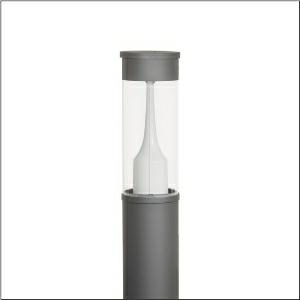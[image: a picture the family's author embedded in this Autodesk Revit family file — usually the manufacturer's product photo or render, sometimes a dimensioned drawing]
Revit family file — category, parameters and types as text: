
# Revit family: city-light_260_iq___st1_2a_5xa5295af14h_a960
name_source: partatom
category: Lighting Fixtures
units: mm (PartAtom-declared; Revit-internal decimal feet)

## family parameters
Cut with Voids When Loaded = No
Host = Face
Light Source = No
Part Type = Normal
Room Calculation Point = No
Round Connector Dimension = Use Diameter
Shared = No

## types (1)
- --- (1 x LED, 1540 lm, 12.9 W, 2200K)
    Apparent Load = 13 VA
    CIE Flux Codes = 22 61 93 96 100
    Color Rendering = 70
    Color Temperature = 2200K
    Default Elevation = 1800 mm
    Description = City-Light 260 iQ, light pillar, Module 540 iQ-SR, primary light control with 3 zone facetted reflector, of plastic, silver coated, highly specular, structured, primary optical cover: cover, of PMMA, transparent, partly coated, light distribution: ST1.2a, primary light characteristic: asymmetric, LED, High Power LED, rated luminous flux: 1.540lm, luminous efficacy: 119lm/W, light colour: 722, colour temperature: 2200K, control gear: iQ Street-Remote, control: pre-setting: logarithmic dimming characteristic, Street-Remote, Auto-Match, Temp-Guard, Lumen-Switch, Night-Set, Smart-Wire, Light-Fading, Desk-Remote (wireless, voltage-free reading and setting of iQ features in the workshop via application-optimized NFC function/RFID function), optimised constant luminous flux control (CLO 2.0), with terminal, 6-pole, max. 2.5mm², mains connection: 230..240V, AC, 50/60Hz, start of lifetime: 13W, end of service life: 13W, reduction: 6W, luminaire housing, cylindrical, of extruded aluminium section, coated, Siteco® metallic grey (DB 702S), length: 2.600mm, diameter: 200mm, Module 540 iQ-SR, traffic white (RAL 9016), equipment: standard, protection rating (complete): IP65, insulation class (complete): insulation class II (safety insulation), certification: CE, ENEC, VDE, packaging unit: 1 piece

Light Distribution: ST1.2a
    Height = 500 mm
    Lamp = 1 x LED
    Lamp Light Flux = 1540 lm
    Lamp Power = 12.9 W
    Lamp count = 1
    Length = 200 mm  [stored 0.656168 ft]
    Luminous efficacy = 119 lm/W
    Manufacturer = Siteco
    ModVariant = No
    Model = 5XA5295AF14H
    Mounting Place = Floor
    Mounting Type = Freestanding
    Number of Poles = 1
    OnlyDefault = Yes
    Power Factor = 1
    Product Name = City-Light 260 iQ | ST1.2a
    Product group = light pillar
    ProductGroupID = 1301
    Protection Class = Protection class II
    Protection Degree = IP 65
    RLX_Detail_Level = 1
    RLX_Emergency_Light_Flux = 0 lm
    RLX_Emergency_Type = 0
    RLX_Emergency_Type_DB = No
    RlxData = <blob elided: 61113 chars, md5=944a0375>
    Socket = socket
    Standby Power = 0 W
    System Light Flux = 1540 lm
    System Power = 13 W
    Type Comments = factory setting: luminous flux: 100 % | dim-lin: 254 | 516 mA
    Type Image = l_1006918.jpg
    URL = http://relux.com
    VarID = @adj_180701
    Voltage = 0 V
    Weight = 0.00 kg
    Width = 0 mm  [stored 0 ft]

note: [stored X ft] marks values corroborated as IEEE doubles in the binary element streams (Revit-internal decimal feet)

## geometry (parser evidence)
native form markers: Blend x4, Sweep x10
no freeform markers — native parametric forms only
